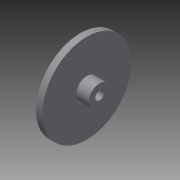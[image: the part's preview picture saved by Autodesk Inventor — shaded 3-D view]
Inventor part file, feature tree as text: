
AUTODESK INVENTOR PART (.ipt)
format: ipt  version: 2013 (Build 170138000, 138)  size: 85,504 bytes
history: native  units: mm
features: extrude x2, sketch x2, other x1
ambient origin geometry x8: Origin, YZ Plane, XZ Plane, XY Plane, X Axis, Y Axis, Z Axis, Center Point
feature tree (5):
  other  "ソリッド1"
  extrude  "押し出し1"  Depth=2.0mm
  extrude  "押し出し2"  Depth=5.0mm
  sketch  "スケッチ1"
  sketch  "スケッチ2"
